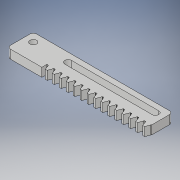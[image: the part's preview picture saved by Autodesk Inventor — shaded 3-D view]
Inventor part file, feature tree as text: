
AUTODESK INVENTOR PART (.ipt)
format: ipt  version: 2019 (Build 230136000, 136)  size: 249,344 bytes
history: native  units: in
note: dims shown in document units (in); Inventor stores cm internally (conversion verified against a paired STEP export)
features: sketch x4, extrude x3, hole x1, pattern_linear x1, fillet x1
ambient origin geometry x8: Origin, YZ Plane, XZ Plane, XY Plane, X Axis, Y Axis, Z Axis, Center Point
bodies: Solid1 (feature_tree)
feature tree (10):
  extrude  "Extrusion1"  Depth=0.5906in
  hole  "Hole2"  [1 undecoded]
  extrude  "Extrusion2"  Depth=0.1969in
  extrude  "Extrusion4"  Depth=0.0787in
  pattern_linear  "Rectangular Pattern1"  Spacing1=0.1969in  [1 undecoded]
  fillet  "Fillet1"  Radius=0.1969in
  sketch  "Sketch1"  dims[d0=3.1496in d1=0.5906in]
  sketch  "Sketch2"  dims[d6=0.1969in d7=0.0in d8=0.1969in]
  sketch  "Sketch3"  dims[d16=0.1969in]
  sketch  "Sketch5"  dims[d17=0.1495in d18=0.2362in d19=0.279in d20=0.0787in d21=0.5635in d22=0.315in d23=0.8108in d24=0.1969in d26=0.2953in d27=0.1969in d28=0.0in d47=0.1969in d48=0.0in d49=0.01in d50=0.01in d51=0.0194in d52=0.0421in d53=0.112in d54=0.1189in d55=0.01in d57=5.9055in d59=0.1571in d60=0.1969in d61=0.1495in d62=0.1495in d63=0.1969in d64=0.1969in d65=1.9685in d68=0.5906in d69=0.2362in d70=0.0787in]
note: 2 required parameter values undecoded (feature->parameter linkage not recoverable at this tier; creation-order binding heuristic only, values carry confidence <= 0.55)
